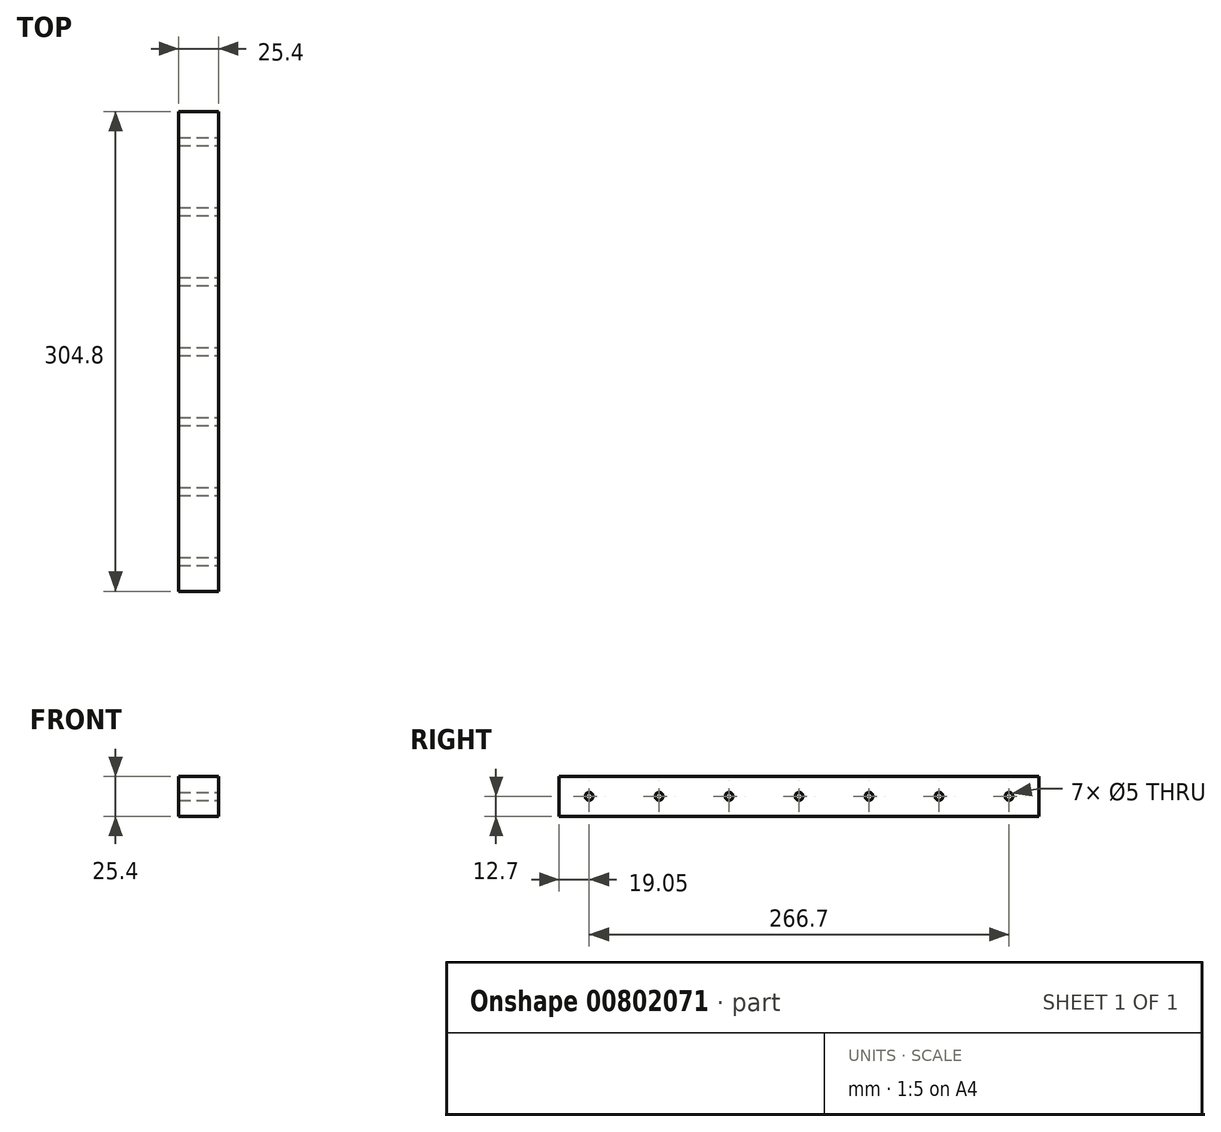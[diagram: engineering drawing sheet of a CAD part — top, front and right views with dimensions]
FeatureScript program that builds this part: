
annotation { "Feature Type Name" : "Feature", "Feature Type Description" : "" }
export const myFeature = defineFeature(function(context is Context, id is Id, definition is map)
    precondition{}
    {
        {
            var Q0;
            Q0=qCreatedBy(makeId("Front.planeOp"),FACE);
            var sketch = newSketch(context, id + "F0", { "sketchPlane" : qUnion([Q0])});
            skLineSegment(sketch, "E0.bottom", {"start": v(12.7, -12.7) * mm, "end": v(-12.7, -12.7) * mm});
            skLineSegment(sketch, "E0.top", {"start": v(12.7, 12.7) * mm, "end": v(-12.7, 12.7) * mm});
            skLineSegment(sketch, "E0.left", {"start": v(12.7, -12.7) * mm, "end": v(12.7, 12.7) * mm});
            skLineSegment(sketch, "E0.right", {"start": v(-12.7, -12.7) * mm, "end": v(-12.7, 12.7) * mm});
            skPoint(sketch, "E0.middle", {"position": v(0, 0) * mm});
            skSolve(sketch);
        }
        {
            var Q0;
            Q0 = qSketchRegion(id + "F0", true);
            extrude(context, id + "F1", {"entities" : qUnion([Q0]), "depth" : 304.8 * mm, "offsetDistance" : 25 * mm});
        }
        {
            var Q0;
            Q0=makeQuery(id+"F1.opExtrude","SWEPT_FACE",FACE,{"disambiguationData":[OSD([sQuery(id+"F0.wireOp",EDGE,"E0.left")])]});
            var sketch = newSketch(context, id + "F2", { "sketchPlane" : qUnion([Q0])});
            skPoint(sketch, "E1", {"position": v(-152.4, 0) * mm});
            skPoint(sketch, "E1.positionSnap0", {"position": v(-152.4, 11.7) * mm});
            skPoint(sketch, "E1.positionSnap1", {"position": v(-304.8, 0) * mm});
            skPoint(sketch, "E2.1.0.0", {"position": v(-107.95, 0) * mm});
            skPoint(sketch, "E2.2.0.0", {"position": v(-63.5, 0) * mm});
            skPoint(sketch, "E2.3.0.0", {"position": v(-19.05, 0) * mm});
            skLineSegment(sketch, "E2.direction1", {"start": v(-152.4, 0) * mm, "end": v(-107.95, 0) * mm, "construction": true});
            skPoint(sketch, "E3.1.0.0", {"position": v(-196.85, 0) * mm});
            skPoint(sketch, "E3.2.0.0", {"position": v(-241.3, 0) * mm});
            skPoint(sketch, "E3.3.0.0", {"position": v(-285.75, 0) * mm});
            skLineSegment(sketch, "E3.direction1", {"start": v(-152.4, 0) * mm, "end": v(-196.85, 0) * mm, "construction": true});
            skSolve(sketch);
        }
        {
            var Q0;
            Q0=sQuery(id+"F2.wireOp",VERTEX,"E3.3.0.0");
            var Q1;
            Q1=sQuery(id+"F2.wireOp",VERTEX,"E3.2.0.0");
            var Q2;
            Q2=sQuery(id+"F2.wireOp",VERTEX,"E3.1.0.0");
            var Q3;
            Q3=sQuery(id+"F2.wireOp",VERTEX,"E1");
            var Q4;
            Q4=sQuery(id+"F2.wireOp",VERTEX,"E2.1.0.0");
            var Q5;
            Q5=sQuery(id+"F2.wireOp",VERTEX,"E2.2.0.0");
            var Q6;
            Q6=sQuery(id+"F2.wireOp",VERTEX,"E2.3.0.0");
            var Q7;
            Q7=makeQuery(id+"F1.opExtrude","SWEPT_BODY",BODY,{"disambiguationData":[OSD([sQuery(id+"F0.wireOp",EDGE,"E0.bottom"),sQuery(id+"F0.wireOp",EDGE,"E0.top"),sQuery(id+"F0.wireOp",EDGE,"E0.left"),sQuery(id+"F0.wireOp",EDGE,"E0.right")])]});
            hole(context, id + "F3", {"style" : HoleStyle.SIMPLE, "endStyle" : HoleEndStyle.THROUGH, "standardTappedOrClearance" : lookupTablePath({ "standard" : "ISO", "engagement" : "75%", "pitch" : "1 mm", "size" : "M6", "type" : "Tapped" }), "standardBlindInLast" : lookupTablePath({ "standard" : "ISO", "fit" : "Normal", "engagement" : "75%", "pitch" : "1 mm", "size" : "M6", "type" : "Clearance & tapped" }), "holeDiameter" : 5 * mm, "majorDiameter" : 6 * mm, "showTappedDepth" : true, "isTappedThrough" : true, "tappedDepth" : 19.05 * mm, "tapClearance" : 3, "startFromSketch" : true, "locations" : qUnion([Q0, Q1, Q2, Q3, Q4, Q5, Q6]), "scope" : qUnion([Q7])});
        }
    });
